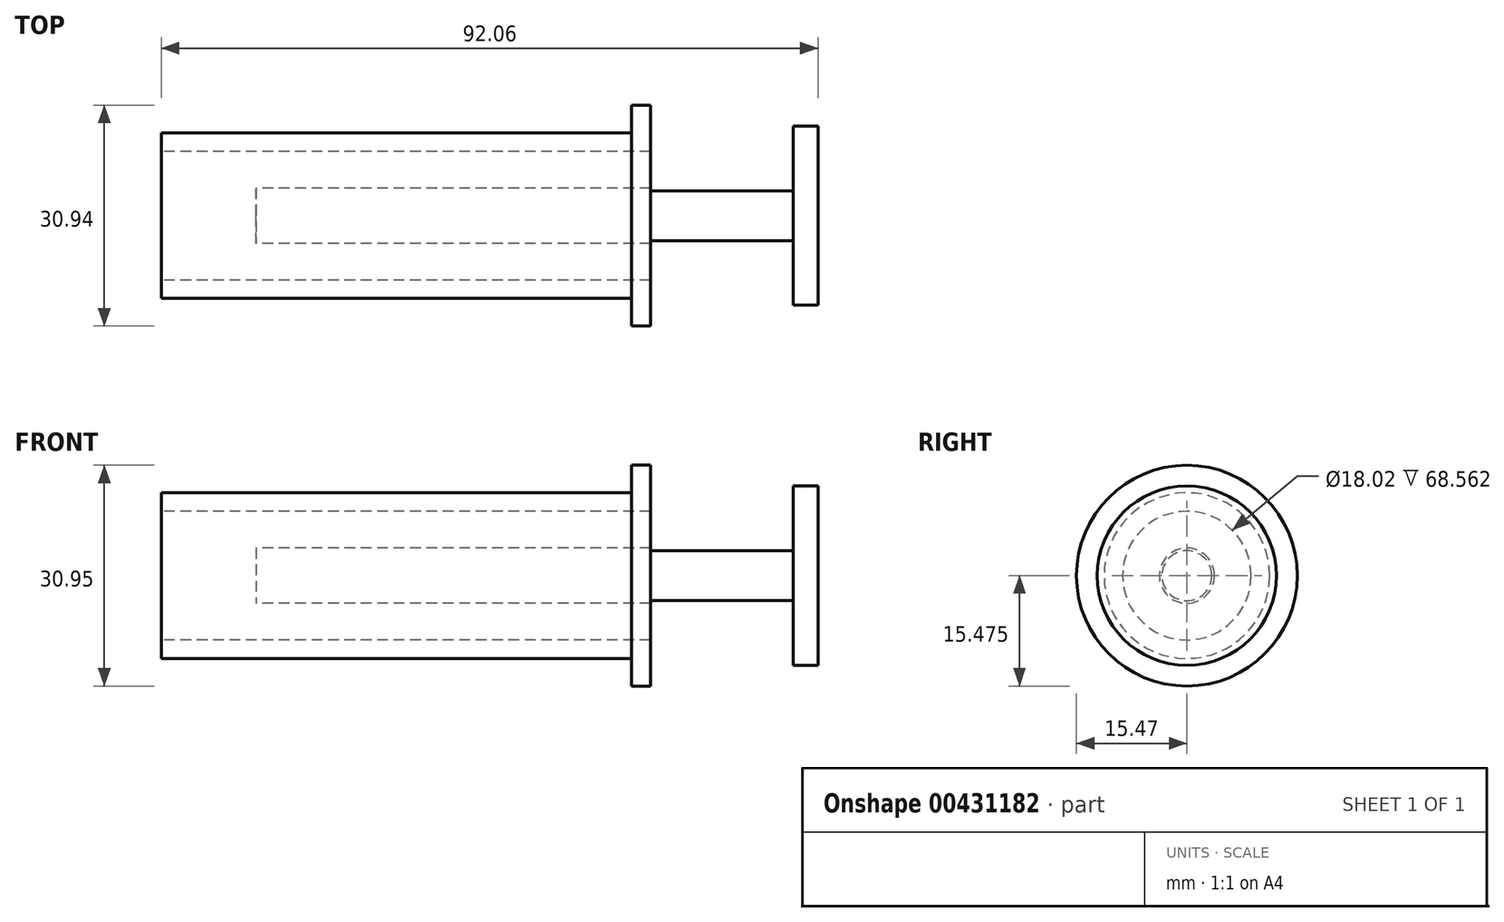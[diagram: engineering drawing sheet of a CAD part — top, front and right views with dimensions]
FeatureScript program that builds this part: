
annotation { "Feature Type Name" : "Feature", "Feature Type Description" : "" }
export const myFeature = defineFeature(function(context is Context, id is Id, definition is map)
    precondition{}
    {
        {
            var Q0;
            Q0=qCreatedBy(makeId("Front.planeOp"),FACE);
            var sketch = newSketch(context, id + "F0", { "sketchPlane" : qUnion([Q0])});
            skLineSegment(sketch, "E0.bottom", {"start": v(-12.57, 3.87) * mm, "end": v(-57.05, 3.87) * mm});
            skLineSegment(sketch, "E0.top", {"start": v(-12.57, -3.87) * mm, "end": v(-57.05, -3.87) * mm});
            skLineSegment(sketch, "E0.left", {"start": v(-12.57, 3.87) * mm, "end": v(-12.57, -3.87) * mm});
            skLineSegment(sketch, "E0.right", {"start": v(-57.05, 3.87) * mm, "end": v(-57.05, -3.87) * mm});
            skPoint(sketch, "E0.middle", {"position": v(-34.8, 0) * mm});
            skLineSegment(sketch, "E1.bottom", {"start": v(-57.05, 3.87) * mm, "end": v(-61.16, 3.87) * mm});
            skLineSegment(sketch, "E1.top", {"start": v(-57.05, -3.87) * mm, "end": v(-61.16, -3.87) * mm});
            skLineSegment(sketch, "E1.right", {"start": v(-61.16, 3.87) * mm, "end": v(-61.16, -3.87) * mm});
            skLineSegment(sketch, "E2.bottom", {"start": v(-61.16, 3.87) * mm, "end": v(-65.26, 3.87) * mm});
            skLineSegment(sketch, "E2.top", {"start": v(-61.16, -3.87) * mm, "end": v(-65.26, -3.87) * mm});
            skLineSegment(sketch, "E2.right", {"start": v(-65.26, 3.87) * mm, "end": v(-65.26, -3.87) * mm});
            skLineSegment(sketch, "E3.bottom", {"start": v(-57.05, 1.2) * mm, "end": v(-12.57, 1.2) * mm});
            skLineSegment(sketch, "E3.top", {"start": v(-57.05, -1.2) * mm, "end": v(-12.57, -1.2) * mm});
            skLineSegment(sketch, "E3.left", {"start": v(-57.05, 1.2) * mm, "end": v(-57.05, -1.2) * mm});
            skLineSegment(sketch, "E3.right", {"start": v(-12.57, 1.2) * mm, "end": v(-12.57, -1.2) * mm});
            skLineSegment(sketch, "E4.bottom", {"start": v(-12.57, 7.74) * mm, "end": v(-9.91, 7.74) * mm});
            skLineSegment(sketch, "E4.top", {"start": v(-12.57, -7.74) * mm, "end": v(-9.91, -7.74) * mm});
            skLineSegment(sketch, "E4.left", {"start": v(-12.57, 7.74) * mm, "end": v(-12.57, -7.74) * mm});
            skLineSegment(sketch, "E4.right", {"start": v(-9.91, 7.74) * mm, "end": v(-9.91, -7.74) * mm});
            skPoint(sketch, "E4.middle", {"position": v(-11.24, 0) * mm});
            skSolve(sketch);
        }
        {
            var Q0;
            Q0 = qSketchRegion(id + "F0", true);
            var Q1;
            Q1=sQuery(id+"F0.wireOp",EDGE,"E4.bottom");
            revolve(context, id + "F1", {"entities" : qUnion([Q0]), "axis" : qUnion([Q1]), "revolveType" : RevolveType.FULL});
        }
        {
            var Q0;
            Q0=makeQuery(id+"F1.opRevolve","SWEPT_FACE",FACE,{"disambiguationData":[OSD([sQuery(id+"F0.wireOp",EDGE,"E4.right")])]});
            var sketch = newSketch(context, id + "F2", { "sketchPlane" : qUnion([Q0])});
            skCircle(sketch, "E5", {"center": v(0, 7.74) * mm, "radius": 3.5 * mm});
            skSolve(sketch);
        }
        {
            var Q0;
            Q0 = qSketchRegion(id + "F2", true);
            extrude(context, id + "F3", {"entities" : qUnion([Q0]), "operationType" : NewBodyOperationType.ADD, "depth" : 20 * mm});
        }
        {
            var Q0;
            Q0=makeQuery(id+"F3.opExtrude","CAP_FACE",FACE,{"disambiguationData":[OSD([sQuery(id+"F2.wireOp",EDGE,"E5")])],"isStart":false});
            var sketch = newSketch(context, id + "F4", { "sketchPlane" : qUnion([Q0])});
            skCircle(sketch, "E6", {"center": v(0, 7.74) * mm, "radius": 12.56 * mm});
            skSolve(sketch);
        }
        {
            var Q0;
            Q0=makeQuery(id+"F4.imprint","IMPRINT",FACE,{"disambiguationData":[TD([[makeQuery(id+"F4.imprint","IMPRINT",EDGE,{"derivedFrom":makeQuery(id+"F3.opExtrude","CAP_EDGE",EDGE,{"disambiguationData":[OSD([sQuery(id+"F2.wireOp",EDGE,"E5")])],"isStart":false})}),1.0]])]});
            var Q1;
            Q1=makeQuery(id+"F4.imprint","IMPRINT",FACE,{"disambiguationData":[TD([[makeQuery(id+"F4.imprint","IMPRINT",EDGE,{"derivedFrom":sQuery(id+"F4.wireOp",EDGE,"E6")}),1.0]])]});
            extrude(context, id + "F5", {"entities" : qUnion([Q0, Q1]), "operationType" : NewBodyOperationType.ADD, "depth" : 3.5 * mm});
        }
        {
            var Q0;
            Q0=makeQuery(id+"F1.opRevolve","SWEPT_FACE",FACE,{"disambiguationData":[OSD([sQuery(id+"F0.wireOp",EDGE,"E2.right")])]});
            var sketch = newSketch(context, id + "F6", { "sketchPlane" : qUnion([Q0])});
            skCircle(sketch, "E7", {"center": v(0, 7.74) * mm, "radius": 9.01 * mm});
            skSolve(sketch);
        }
        {
            var Q0;
            Q0=makeQuery(id+"F6.imprint","IMPRINT",FACE,{"disambiguationData":[TD([[makeQuery(id+"F6.imprint","IMPRINT",EDGE,{"derivedFrom":sQuery(id+"F6.wireOp",EDGE,"E7")}),1.0]])]});
            extrude(context, id + "F7", {"entities" : qUnion([Q0]), "operationType" : NewBodyOperationType.REMOVE, "oppositeDirection" : true, "depth" : 61.72 * mm});
        }
        {
            var Q0;
            {var subQ0=sQuery(id+"F0.wireOp",EDGE,"E4.left");Q0=makeQuery(id+"F1.opRevolve","SWEPT_FACE",FACE,{"disambiguationData":[OSD([subQ0]),TDD([makeQuery(id+"F0.imprint","IMPRINT",EDGE,{"disambiguationData":[TD([[makeQuery(id+"F0.imprint","INTERSECT",VERTEX,{"derivedFrom":[sQuery(id+"F0.wireOp",EDGE,"E0.bottom"),subQ0]}),1.0]])],"derivedFrom":subQ0})])]});}
            extrude(context, id + "F8", {"entities" : qUnion([Q0]), "operationType" : NewBodyOperationType.ADD, "depth" : 52.63 * mm});
        }
        {
            var Q0;
            Q0=makeQuery(id+"F1.opRevolve","SWEPT_FACE",FACE,{"disambiguationData":[OSD([sQuery(id+"F0.wireOp",EDGE,"E2.right")])]});
            extrude(context, id + "F9", {"entities" : qUnion([Q0]), "operationType" : NewBodyOperationType.ADD, "depth" : 13.2 * mm});
        }
    });
